# Revit family: Combination-Willoughby-ECW-1846-R-ON
name_source: partatom
category: Plumbing Fixtures
revit_build: Autodesk Revit 2015 (Build: 20140606_1530(x64)
units: mm (PartAtom-declared; Revit-internal decimal feet)

## types (2) — shared parameters
CW Connection = No
Default Elevation = 0' - 0"
Flush Inlet Connection = Yes
Flush Inlet DIA = 2"
HW Connection = No
Lav Waste Connection = Yes
Lav Waste DIA = 2"
Manufacturer = Willoughby Industries
Vent Connection = No
Waste DIA = 2"

## per-type parameters (varying)
| type | Description | Fixture Body | Model | Type Comments | URL | Waste Connection | revision |
| Left | High Efficiency Combination Unit | <By Category> | ECW-1846-HET-L-ON | Bowl Location | www.willoughby-ind.com | No |  |
| Standard | 1846 Combination Unit, Wall toilet outlet, Right toilet, On Floor mounted | Stainless Steel AISI 304-Willoughby | ECW-1846-R-ON |  | https://www.willoughby-ind.com | Yes | A |

## geometry (parser evidence)
native form markers: Sweep x2
no freeform markers — native parametric forms only
